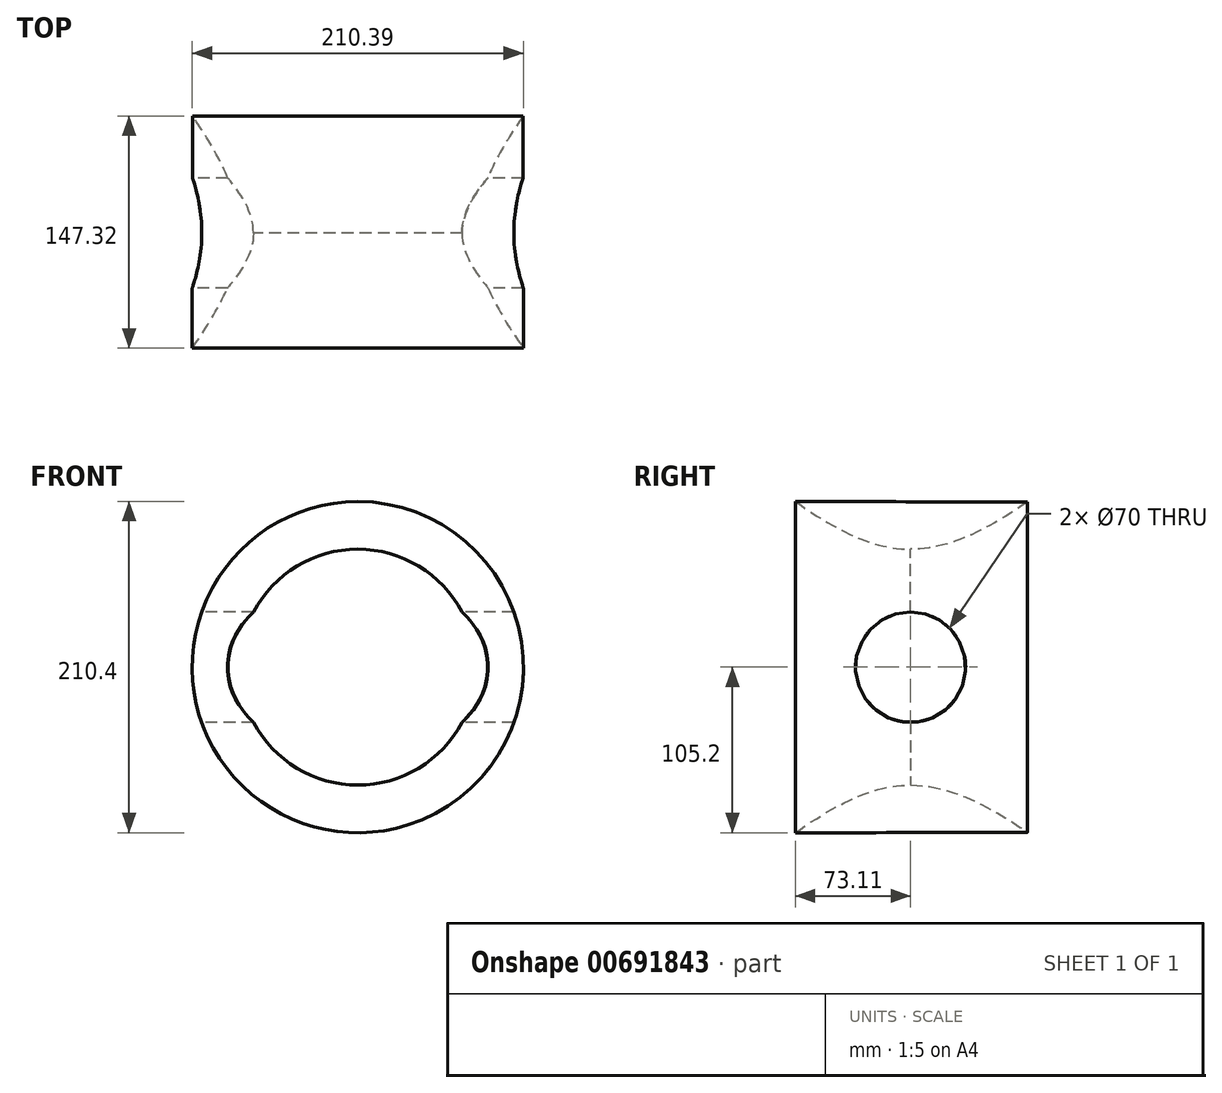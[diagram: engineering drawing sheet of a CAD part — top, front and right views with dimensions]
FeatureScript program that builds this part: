
annotation { "Feature Type Name" : "Feature", "Feature Type Description" : "" }
export const myFeature = defineFeature(function(context is Context, id is Id, definition is map)
    precondition{}
    {
        {
            var Q0;
            Q0=qCreatedBy(makeId("Right.planeOp"),FACE);
            var sketch = newSketch(context, id + "F0", { "sketchPlane" : qUnion([Q0])});
            skLineSegment(sketch, "E0", {"start": v(-73.1, -73.84) * mm, "end": v(0, 0) * mm});
            skLineSegment(sketch, "E1", {"start": v(0, 0) * mm, "end": v(74.2, -73.48) * mm});
            skLineSegment(sketch, "E2", {"start": v(74.2, -73.48) * mm, "end": v(-73.1, -73.84) * mm});
            skSolve(sketch);
        }
        {
            var Q0;
            Q0=qCreatedBy(makeId("Top.planeOp"),FACE);
            var sketch = newSketch(context, id + "F1", { "sketchPlane" : qUnion([Q0])});
            skLineSegment(sketch, "E3", {"start": v(73.1, 74.56) * mm, "end": v(-74.93, 74.56) * mm});
            skLineSegment(sketch, "E4", {"start": v(-74.93, 74.56) * mm, "end": v(-74.93, -59.96) * mm});
            skSolve(sketch);
        }
        {
            var Q0;
            Q0 = qSketchRegion(id + "F0", true);
            var Q1;
            Q1=sQuery(id+"F1.wireOp",EDGE,"E4");
            revolve(context, id + "F2", {"entities" : qUnion([Q0]), "axis" : qUnion([Q1]), "revolveType" : RevolveType.FULL});
        }
        {
            var Q0;
            Q0=qCreatedBy(makeId("Right.planeOp"),FACE);
            var sketch = newSketch(context, id + "F3", { "sketchPlane" : qUnion([Q0])});
            skCircle(sketch, "E5", {"center": v(0, 0) * mm, "radius": 35 * mm});
            skSolve(sketch);
        }
        {
            var Q0;
            Q0 = qSketchRegion(id + "F3", true);
            extrude(context, id + "F4", {"entities" : qUnion([Q0]), "operationType" : NewBodyOperationType.REMOVE, "endBound" : BoundingType.THROUGH_ALL, "depth" : 25 * mm, "offsetDistance" : 25 * mm, "hasSecondDirection" : true, "secondDirectionBound" : SecondDirectionBoundingType.THROUGH_ALL, "secondDirectionOppositeDirection" : true, "secondDirectionDepth" : 25 * mm});
        }
    });
